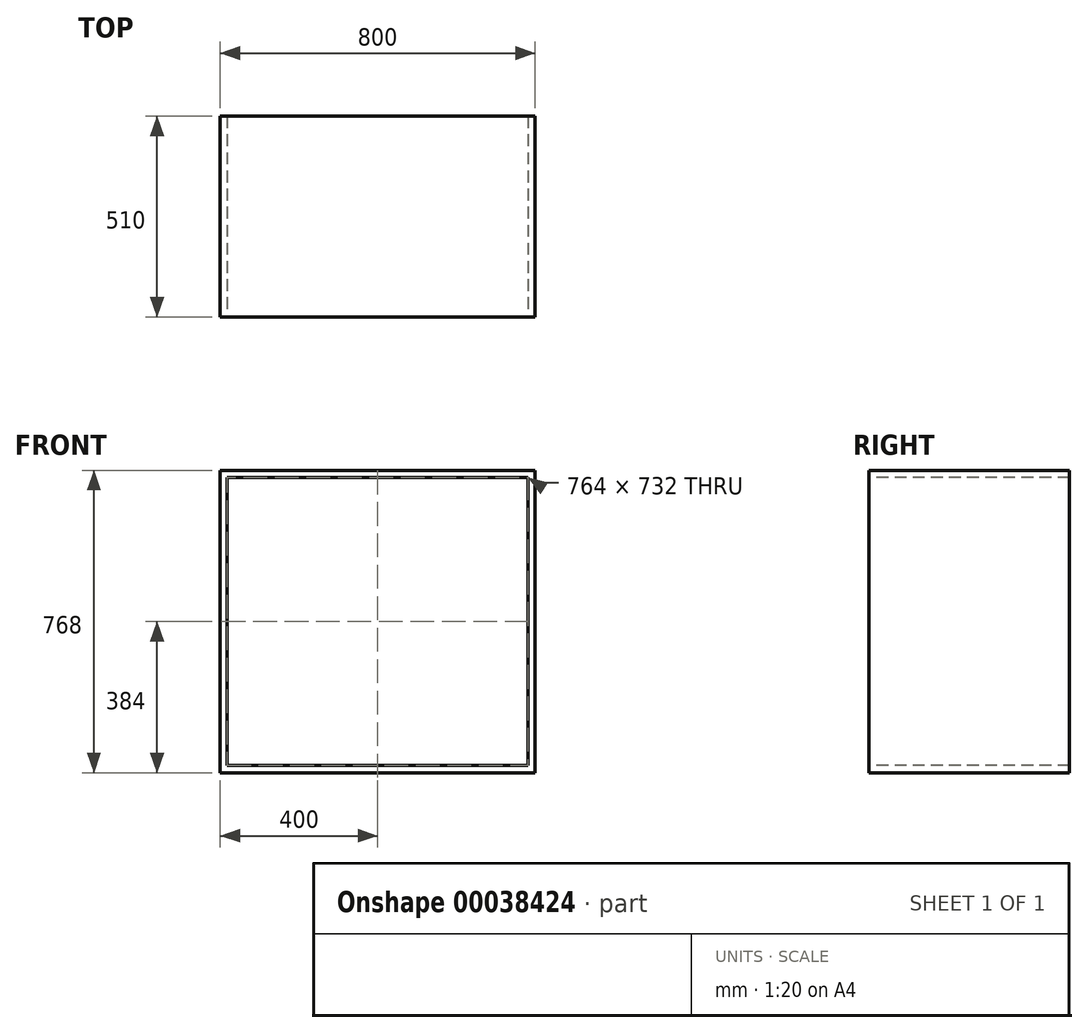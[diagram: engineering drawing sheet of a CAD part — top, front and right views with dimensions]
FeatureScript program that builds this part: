
annotation { "Feature Type Name" : "Feature", "Feature Type Description" : "" }
export const myFeature = defineFeature(function(context is Context, id is Id, definition is map)
    precondition{}
    {
        {
            var Q0;
            Q0=qCreatedBy(makeId("Top.planeOp"),FACE);
            var sketch = newSketch(context, id + "F0", { "sketchPlane" : qUnion([Q0])});
            skLineSegment(sketch, "E0.rect.bottom", {"start": v(-400, -255) * mm, "end": v(400, -255) * mm});
            skLineSegment(sketch, "E0.rect.top", {"start": v(-400, 255) * mm, "end": v(400, 255) * mm});
            skLineSegment(sketch, "E0.rect.left", {"start": v(-400, -255) * mm, "end": v(-400, 255) * mm});
            skLineSegment(sketch, "E0.rect.right", {"start": v(400, -255) * mm, "end": v(400, 255) * mm});
            skPoint(sketch, "E0.rect.middle", {"position": v(0, 0) * mm});
            skSolve(sketch);
        }
        {
            var Q0;
            Q0=makeQuery(id+"F0.imprint","IMPRINT",FACE,{"disambiguationData":[TD([[makeQuery(id+"F0.imprint","IMPRINT",EDGE,{"derivedFrom":sQuery(id+"F0.wireOp",EDGE,"E0.rect.bottom")}),1.0]])]});
            extrude(context, id + "F1", {"entities" : qUnion([Q0]), "depth" : 18 * mm});
        }
        {
            var Q0;
            Q0=makeQuery(id+"F1.opExtrude","CAP_FACE",FACE,{"disambiguationData":[OSD([sQuery(id+"F0.wireOp",EDGE,"E0.rect.bottom"),sQuery(id+"F0.wireOp",EDGE,"E0.rect.top"),sQuery(id+"F0.wireOp",EDGE,"E0.rect.left"),sQuery(id+"F0.wireOp",EDGE,"E0.rect.right")])],"isStart":false});
            var sketch = newSketch(context, id + "F2", { "sketchPlane" : qUnion([Q0])});
            skLineSegment(sketch, "E1.bottom", {"start": v(-400, 255) * mm, "end": v(-382, 255) * mm});
            skLineSegment(sketch, "E1.top", {"start": v(-400, -255) * mm, "end": v(-382, -255) * mm});
            skLineSegment(sketch, "E1.left", {"start": v(-400, 255) * mm, "end": v(-400, -255) * mm});
            skLineSegment(sketch, "E1.right", {"start": v(-382, 255) * mm, "end": v(-382, -255) * mm});
            skSolve(sketch);
        }
        {
            var Q0;
            Q0=makeQuery(id+"F2.imprint","IMPRINT",FACE,{"disambiguationData":[TD([[makeQuery(id+"F2.imprint","IMPRINT",EDGE,{"derivedFrom":sQuery(id+"F2.wireOp",EDGE,"E1.bottom")}),-1.0]])]});
            extrude(context, id + "F3", {"entities" : qUnion([Q0]), "operationType" : NewBodyOperationType.ADD, "depth" : 750 * mm});
        }
        {
            var Q0;
            Q0=makeQuery(id+"F1.opExtrude","CAP_FACE",FACE,{"disambiguationData":[OSD([sQuery(id+"F0.wireOp",EDGE,"E0.rect.bottom"),sQuery(id+"F0.wireOp",EDGE,"E0.rect.top"),sQuery(id+"F0.wireOp",EDGE,"E0.rect.left"),sQuery(id+"F0.wireOp",EDGE,"E0.rect.right")])],"isStart":false});
            var sketch = newSketch(context, id + "F4", { "sketchPlane" : qUnion([Q0])});
            skLineSegment(sketch, "E2.bottom", {"start": v(400, 255) * mm, "end": v(382, 255) * mm});
            skLineSegment(sketch, "E2.top", {"start": v(400, -255) * mm, "end": v(382, -255) * mm});
            skLineSegment(sketch, "E2.left", {"start": v(400, 255) * mm, "end": v(400, -255) * mm});
            skLineSegment(sketch, "E2.right", {"start": v(382, 255) * mm, "end": v(382, -255) * mm});
            skSolve(sketch);
        }
        {
            var Q0;
            Q0=makeQuery(id+"F4.imprint","IMPRINT",FACE,{"disambiguationData":[TD([[makeQuery(id+"F4.imprint","IMPRINT",EDGE,{"derivedFrom":sQuery(id+"F4.wireOp",EDGE,"E2.bottom")}),-1.0]])]});
            extrude(context, id + "F5", {"entities" : qUnion([Q0]), "operationType" : NewBodyOperationType.ADD, "depth" : 750 * mm});
        }
        {
            var Q0;
            Q0=makeQuery(id+"F5.opExtrude","SWEPT_FACE",FACE,{"disambiguationData":[OSD([sQuery(id+"F4.wireOp",EDGE,"E2.right")])]});
            var sketch = newSketch(context, id + "F6", { "sketchPlane" : qUnion([Q0])});
            skLineSegment(sketch, "E3.bottom", {"start": v(-255, 768) * mm, "end": v(255, 768) * mm});
            skLineSegment(sketch, "E3.top", {"start": v(-255, 750) * mm, "end": v(255, 750) * mm});
            skLineSegment(sketch, "E3.left", {"start": v(-255, 768) * mm, "end": v(-255, 750) * mm});
            skLineSegment(sketch, "E3.right", {"start": v(255, 768) * mm, "end": v(255, 750) * mm});
            skSolve(sketch);
        }
        {
            var Q0;
            Q0=makeQuery(id+"F6.imprint","IMPRINT",FACE,{"disambiguationData":[TD([[makeQuery(id+"F6.imprint","IMPRINT",EDGE,{"derivedFrom":sQuery(id+"F6.wireOp",EDGE,"E3.bottom")}),-1.0]])]});
            extrude(context, id + "F7", {"entities" : qUnion([Q0]), "operationType" : NewBodyOperationType.ADD, "depth" : 764 * mm});
        }
    });
